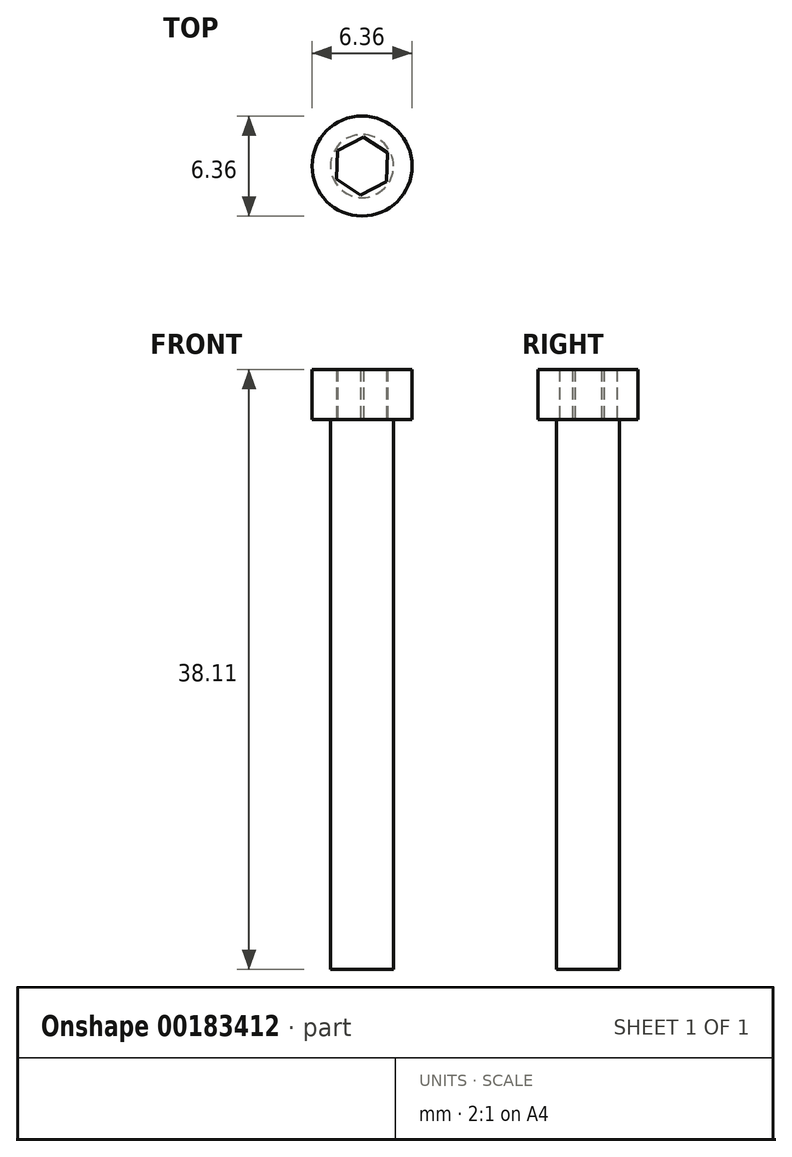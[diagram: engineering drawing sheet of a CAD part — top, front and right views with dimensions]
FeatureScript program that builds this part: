
annotation { "Feature Type Name" : "Feature", "Feature Type Description" : "" }
export const myFeature = defineFeature(function(context is Context, id is Id, definition is map)
    precondition{}
    {
        {
            var Q0;
            Q0=qCreatedBy(makeId("Top.planeOp"),FACE);
            var sketch = newSketch(context, id + "F0", { "sketchPlane" : qUnion([Q0])});
            skCircle(sketch, "E0", {"center": v(0, 0) * mm, "radius": 3.18 * mm});
            skLineSegment(sketch, "E1.0", {"start": v(0.09, 1.83) * mm, "end": v(1.63, 0.84) * mm});
            skLineSegment(sketch, "E1.1", {"start": v(1.63, 0.84) * mm, "end": v(1.54, -1) * mm});
            skLineSegment(sketch, "E1.2", {"start": v(1.54, -1) * mm, "end": v(-0.09, -1.83) * mm});
            skLineSegment(sketch, "E1.3", {"start": v(-0.09, -1.83) * mm, "end": v(-1.63, -0.84) * mm});
            skLineSegment(sketch, "E1.4", {"start": v(-1.63, -0.84) * mm, "end": v(-1.54, 1) * mm});
            skLineSegment(sketch, "E1.5", {"start": v(-1.54, 1) * mm, "end": v(0.09, 1.83) * mm});
            skPoint(sketch, "E1.0.midPoint", {"position": v(0.86, 1.34) * mm});
            skSolve(sketch);
        }
        {
            var Q0;
            Q0=makeQuery(id+"F0.imprint","IMPRINT",FACE,{"disambiguationData":[TD([[makeQuery(id+"F0.imprint","IMPRINT",EDGE,{"derivedFrom":sQuery(id+"F0.wireOp",EDGE,"E0")}),1.0]])]});
            extrude(context, id + "F1", {"entities" : qUnion([Q0]), "depth" : 3.17 * mm});
        }
        {
            var Q0;
            Q0=makeQuery(id+"F0.imprint","IMPRINT",FACE,{"disambiguationData":[TD([[makeQuery(id+"F0.imprint","IMPRINT",EDGE,{"derivedFrom":sQuery(id+"F0.wireOp",EDGE,"E1.0")}),-1.0]])]});
            var sketch = newSketch(context, id + "F2", { "sketchPlane" : qUnion([Q0])});
            skCircle(sketch, "E2", {"center": v(0, 0) * mm, "radius": 2 * mm});
            skSolve(sketch);
        }
        {
            var Q0;
            Q0=makeQuery(id+"F2.imprint","IMPRINT",FACE,{"disambiguationData":[TD([[makeQuery(id+"F2.imprint","IMPRINT",EDGE,{"derivedFrom":sQuery(id+"F2.wireOp",EDGE,"E2")}),1.0]])]});
            var Q1;
            Q1=makeQuery(id+"F0.imprint","IMPRINT",FACE,{"disambiguationData":[TD([[makeQuery(id+"F0.imprint","IMPRINT",EDGE,{"derivedFrom":sQuery(id+"F0.wireOp",EDGE,"E1.0")}),-1.0]])]});
            extrude(context, id + "F3", {"entities" : qUnion([Q0, Q1]), "operationType" : NewBodyOperationType.ADD, "oppositeDirection" : true, "depth" : 34.92 * mm});
        }
    });
